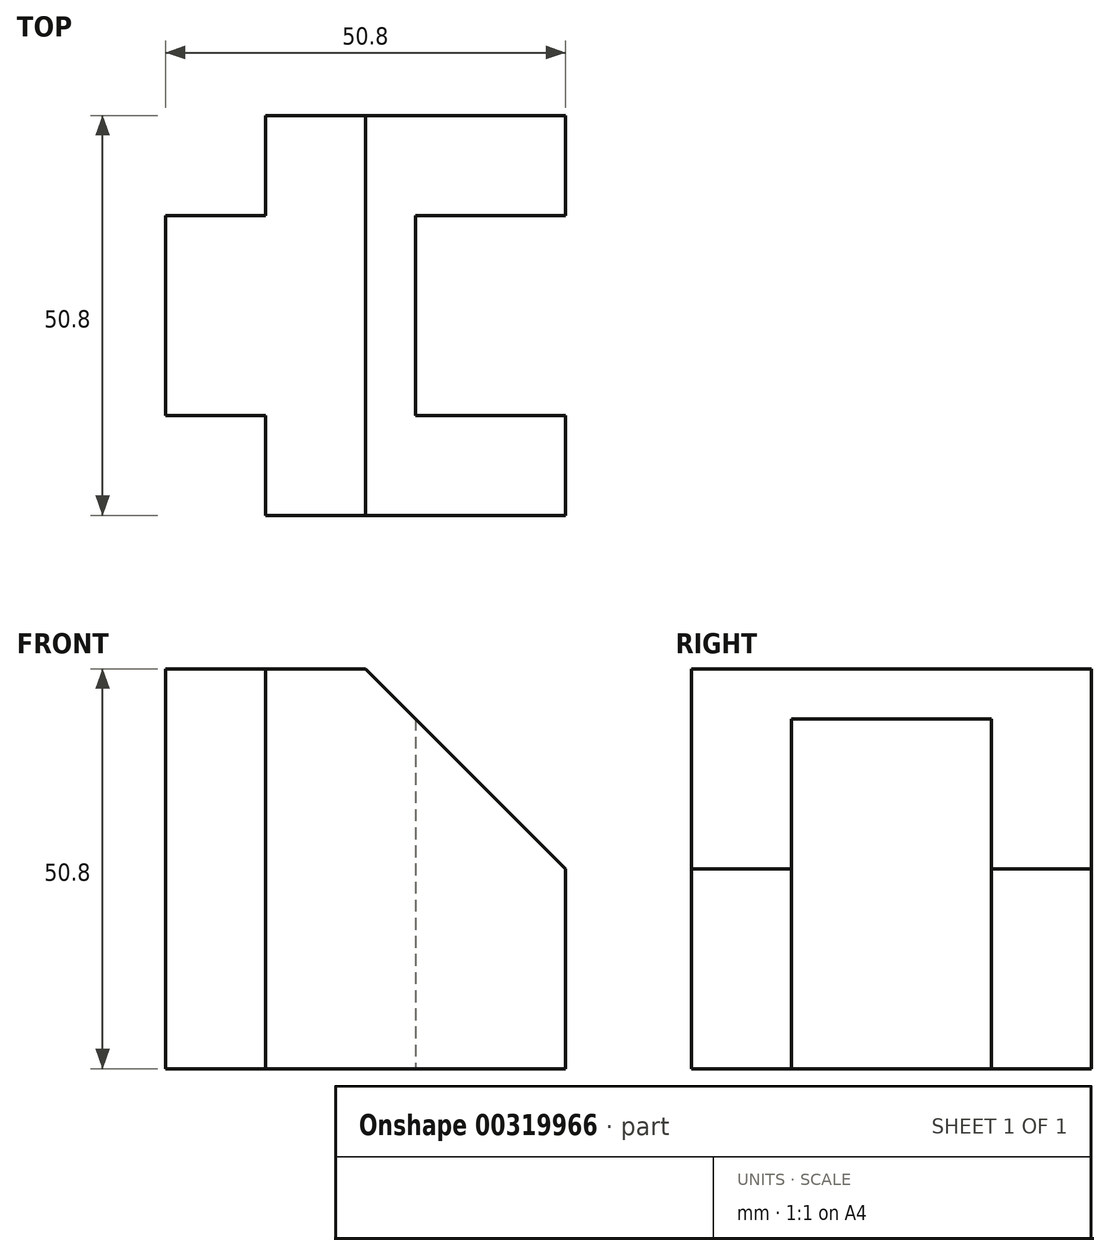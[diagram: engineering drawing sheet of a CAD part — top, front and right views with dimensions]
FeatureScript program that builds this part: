
annotation { "Feature Type Name" : "Feature", "Feature Type Description" : "" }
export const myFeature = defineFeature(function(context is Context, id is Id, definition is map)
    precondition{}
    {
        {
            var Q0;
            Q0=qCreatedBy(makeId("Top.planeOp"),FACE);
            var sketch = newSketch(context, id + "F0", { "sketchPlane" : qUnion([Q0])});
            skLineSegment(sketch, "E0", {"start": v(0, 0) * mm, "end": v(25.4, 0) * mm});
            skLineSegment(sketch, "E1", {"start": v(25.4, 0) * mm, "end": v(25.4, 12.7) * mm});
            skLineSegment(sketch, "E2", {"start": v(25.4, 12.7) * mm, "end": v(6.35, 12.7) * mm});
            skLineSegment(sketch, "E3", {"start": v(6.35, 12.7) * mm, "end": v(6.35, 38.1) * mm});
            skLineSegment(sketch, "E4", {"start": v(6.35, 38.1) * mm, "end": v(25.4, 38.1) * mm});
            skLineSegment(sketch, "E5", {"start": v(25.4, 38.1) * mm, "end": v(25.4, 50.8) * mm});
            skLineSegment(sketch, "E6", {"start": v(25.4, 50.8) * mm, "end": v(0, 50.8) * mm});
            skLineSegment(sketch, "E7", {"start": v(0, 50.8) * mm, "end": v(0, 0) * mm});
            skLineSegment(sketch, "E8", {"start": v(0, 50.8) * mm, "end": v(-12.7, 50.8) * mm});
            skLineSegment(sketch, "E9", {"start": v(-12.7, 50.8) * mm, "end": v(-12.7, 38.1) * mm});
            skLineSegment(sketch, "E10", {"start": v(-12.7, 38.1) * mm, "end": v(-25.4, 38.1) * mm});
            skLineSegment(sketch, "E11", {"start": v(-25.4, 38.1) * mm, "end": v(-25.4, 12.7) * mm});
            skLineSegment(sketch, "E12", {"start": v(-25.4, 12.7) * mm, "end": v(-12.7, 12.7) * mm});
            skLineSegment(sketch, "E13", {"start": v(-12.7, 12.7) * mm, "end": v(-12.7, 0) * mm});
            skLineSegment(sketch, "E14", {"start": v(-12.7, 0) * mm, "end": v(0, 0) * mm});
            skSolve(sketch);
        }
        {
            var Q0;
            Q0=makeQuery(id+"F0.imprint","IMPRINT",FACE,{"disambiguationData":[TD([[makeQuery(id+"F0.imprint","IMPRINT",EDGE,{"derivedFrom":sQuery(id+"F0.wireOp",EDGE,"E7")}),-1.0]])]});
            extrude(context, id + "F1", {"entities" : qUnion([Q0]), "depth" : 50.8 * mm});
        }
        {
            var Q0;
            Q0=makeQuery(id+"F0.imprint","IMPRINT",FACE,{"disambiguationData":[TD([[makeQuery(id+"F0.imprint","IMPRINT",EDGE,{"derivedFrom":sQuery(id+"F0.wireOp",EDGE,"E0")}),1.0]])]});
            extrude(context, id + "F2", {"entities" : qUnion([Q0]), "operationType" : NewBodyOperationType.ADD, "depth" : 25.4 * mm});
        }
        {
            var Q0;
            Q0=makeQuery(id+"F2.boolean.opBoolean","MERGE",FACE,{"derivedFrom":[makeQuery(id+"F1.opExtrude","SWEPT_FACE",FACE,{"disambiguationData":[OSD([sQuery(id+"F0.wireOp",EDGE,"E14")])]}),makeQuery(id+"F2.opExtrude","SWEPT_FACE",FACE,{"disambiguationData":[OSD([sQuery(id+"F0.wireOp",EDGE,"E0")])]})]});
            var sketch = newSketch(context, id + "F3", { "sketchPlane" : qUnion([Q0])});
            skLineSegment(sketch, "E15", {"start": v(0, 50.8) * mm, "end": v(25.4, 25.4) * mm});
            skLineSegment(sketch, "E16", {"start": v(25.4, 25.4) * mm, "end": v(0, 25.4) * mm});
            skLineSegment(sketch, "E17", {"start": v(0, 25.4) * mm, "end": v(0, 50.8) * mm});
            skSolve(sketch);
        }
        {
            var Q0;
            Q0 = qSketchRegion(id + "F3", true);
            extrude(context, id + "F4", {"entities" : qUnion([Q0]), "operationType" : NewBodyOperationType.ADD, "oppositeDirection" : true, "depth" : 50.8 * mm});
        }
        {
            var Q0;
            Q0=makeQuery(id+"F4.opExtrude","SWEPT_FACE",FACE,{"disambiguationData":[OSD([sQuery(id+"F3.wireOp",EDGE,"E16")])]});
            var sketch = newSketch(context, id + "F5", { "sketchPlane" : qUnion([Q0])});
            skLineSegment(sketch, "E18", {"start": v(25.4, -12.7) * mm, "end": v(6.35, -12.7) * mm});
            skLineSegment(sketch, "E19", {"start": v(6.35, -12.7) * mm, "end": v(6.35, -38.1) * mm});
            skLineSegment(sketch, "E20", {"start": v(6.35, -38.1) * mm, "end": v(25.4, -38.1) * mm});
            skLineSegment(sketch, "E21", {"start": v(25.4, -38.1) * mm, "end": v(25.4, -12.7) * mm});
            skSolve(sketch);
        }
        {
            var Q0;
            Q0 = qSketchRegion(id + "F5", true);
            extrude(context, id + "F6", {"entities" : qUnion([Q0]), "operationType" : NewBodyOperationType.REMOVE, "endBound" : BoundingType.THROUGH_ALL, "oppositeDirection" : true, "depth" : 25.4 * mm});
        }
    });
